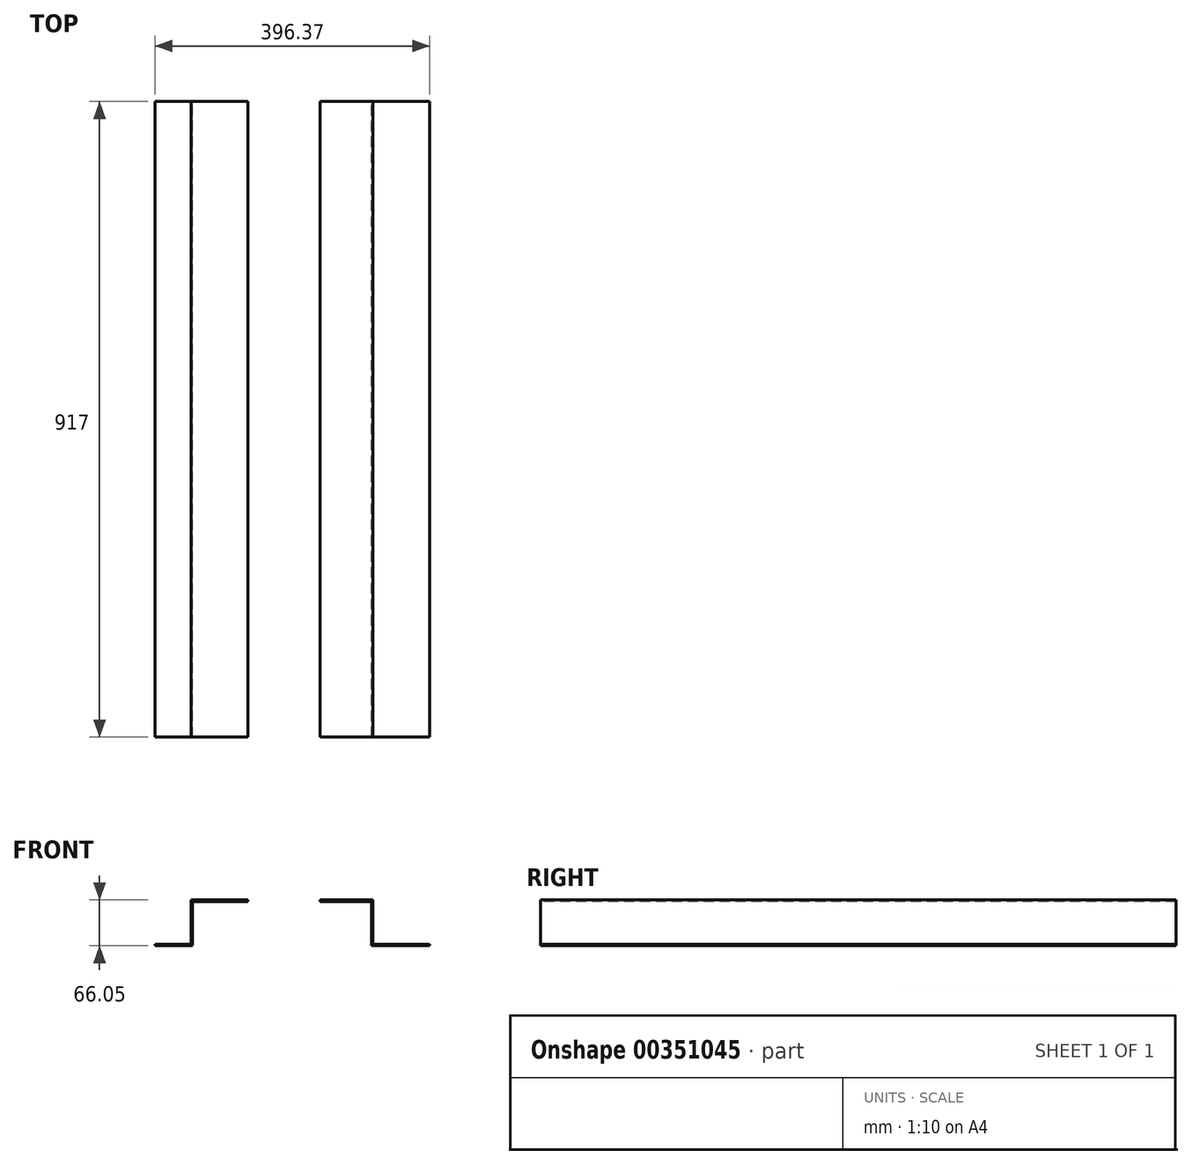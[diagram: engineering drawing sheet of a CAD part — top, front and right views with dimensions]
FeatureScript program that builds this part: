
annotation { "Feature Type Name" : "Feature", "Feature Type Description" : "" }
export const myFeature = defineFeature(function(context is Context, id is Id, definition is map)
    precondition{}
    {
        {
            var Q0;
            Q0=qCreatedBy(makeId("Front.planeOp"),FACE);
            var sketch = newSketch(context, id + "F0", { "sketchPlane" : qUnion([Q0])});
            skLineSegment(sketch, "E0.top", {"start": v(211.5, -66.05) * mm, "end": v(133.36, -66.05) * mm});
            skPoint(sketch, "E0.middle", {"position": v(0, 0) * mm});
            skLineSegment(sketch, "E1.bottom", {"start": v(211.5, -64.05) * mm, "end": v(129.5, -64.05) * mm});
            skLineSegment(sketch, "E2", {"start": v(-132.88, 0) * mm, "end": v(129.5, 0) * mm});
            skLineSegment(sketch, "E3", {"start": v(-184.88, -64.05) * mm, "end": v(-184.88, -66.05) * mm});
            skLineSegment(sketch, "E4", {"start": v(211.5, -64.05) * mm, "end": v(211.5, -66.05) * mm});
            skPoint(sketch, "E0.right.start.orphan", {"position": v(-221, 66.05) * mm});
            skPoint(sketch, "E5.orphan", {"position": v(-221, -66.05) * mm});
            skLineSegment(sketch, "E6", {"start": v(-132.88, 0) * mm, "end": v(-132.88, -64.05) * mm});
            skLineSegment(sketch, "E7", {"start": v(129.5, 0) * mm, "end": v(129.5, -64.05) * mm});
            skLineSegment(sketch, "E8.trimOffspring", {"start": v(-132.88, -64.05) * mm, "end": v(-184.88, -64.05) * mm});
            skLineSegment(sketch, "E9.trimOffspring", {"start": v(-133.36, -66.05) * mm, "end": v(-184.88, -66.05) * mm});
            skLineSegment(sketch, "E10.top", {"start": v(-130.88, -2) * mm, "end": v(127.5, -2) * mm});
            skLineSegment(sketch, "E10.left", {"start": v(-130.88, -66.05) * mm, "end": v(-130.88, -2) * mm});
            skLineSegment(sketch, "E10.right", {"start": v(127.5, -66.05) * mm, "end": v(127.5, -2) * mm});
            skLineSegment(sketch, "E11", {"start": v(-133.36, -66.05) * mm, "end": v(-130.88, -66.05) * mm});
            skLineSegment(sketch, "E12", {"start": v(127.5, -66.05) * mm, "end": v(133.36, -66.05) * mm});
            skSolve(sketch);
        }
        {
            var Q0;
            Q0=qSketchRegion(id+"F0",true);
            extrude(context, id + "F1", {"entities" : qUnion([Q0]), "depth" : 917 * mm});
        }
        {
            var Q0;
            Q0=qCreatedBy(makeId("Top.planeOp"),FACE);
            var sketch = newSketch(context, id + "F2", { "sketchPlane" : qUnion([Q0])});
            skLineSegment(sketch, "E13.top", {"start": v(-51.16, 0) * mm, "end": v(53.15, 0) * mm});
            skLineSegment(sketch, "E13.left", {"start": v(-51.16, -198.7) * mm, "end": v(-51.16, 0) * mm});
            skLineSegment(sketch, "E13.right", {"start": v(53.15, -198.7) * mm, "end": v(53.15, 0) * mm});
            skPoint(sketch, "E13.middle", {"position": v(1, -99.35) * mm});
            skLineSegment(sketch, "E14.MirrorCS", {"start": v(53.15, -718.3) * mm, "end": v(53.15, -917) * mm});
            skLineSegment(sketch, "E15.MirrorCS", {"start": v(-51.16, -718.3) * mm, "end": v(-51.16, -917) * mm});
            skLineSegment(sketch, "E16.MirrorCS", {"start": v(-51.16, -917) * mm, "end": v(53.15, -917) * mm});
            skPoint(sketch, "E17.MirrorP", {"position": v(1, -819.16) * mm});
            skPoint(sketch, "E18.middle", {"position": v(0, -448.67) * mm});
            skLineSegment(sketch, "E19", {"start": v(-51.16, -718.3) * mm, "end": v(-51.16, -190.44) * mm});
            skLineSegment(sketch, "E20", {"start": v(53.15, -718.3) * mm, "end": v(53.15, -198.7) * mm});
            skSolve(sketch);
        }
        {
            var Q0;
            Q0=makeQuery(id+"F2.imprint","IMPRINT",FACE,{"disambiguationData":[TD([[makeQuery(id+"F2.imprint","IMPRINT",EDGE,{"derivedFrom":sQuery(id+"F2.wireOp",EDGE,"E13.bottom")}),1.0]])]});
            var Q1;
            Q1=makeQuery(id+"F2.imprint","IMPRINT",FACE,{"disambiguationData":[TD([[makeQuery(id+"F2.imprint","IMPRINT",EDGE,{"derivedFrom":sQuery(id+"F2.wireOp",EDGE,"E18.bottom")}),1.0]])]});
            var Q2;
            Q2=makeQuery(id+"F2.imprint","IMPRINT",FACE,{"disambiguationData":[TD([[makeQuery(id+"F2.imprint","IMPRINT",EDGE,{"derivedFrom":sQuery(id+"F2.wireOp",EDGE,"E14.MirrorCS")}),-1.0]])]});
            extrude(context, id + "F3", {"entities" : qUnion([Q0, Q1, Q2]), "operationType" : NewBodyOperationType.REMOVE, "oppositeDirection" : true, "depth" : 2 * mm});
        }
    });
